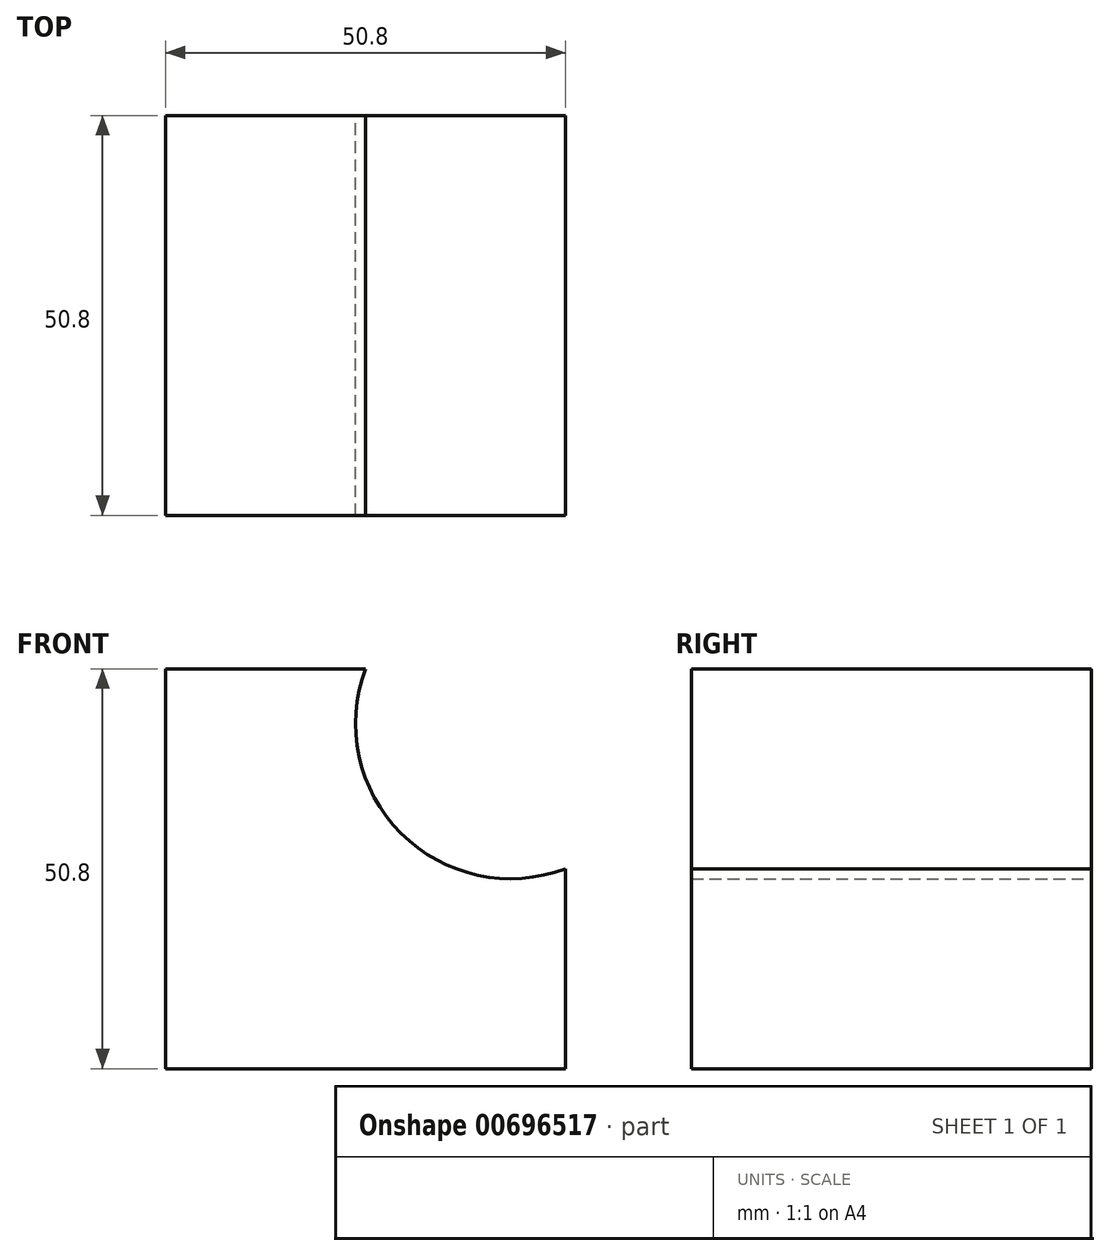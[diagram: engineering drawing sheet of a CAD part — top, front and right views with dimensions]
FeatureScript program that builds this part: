
annotation { "Feature Type Name" : "Feature", "Feature Type Description" : "" }
export const myFeature = defineFeature(function(context is Context, id is Id, definition is map)
    precondition{}
    {
        {
            var Q0;
            Q0=qCreatedBy(makeId("Front.planeOp"),FACE);
            var sketch = newSketch(context, id + "F0", { "sketchPlane" : qUnion([Q0])});
            skLineSegment(sketch, "E0", {"start": v(0, 0) * mm, "end": v(0, -50.8) * mm});
            skLineSegment(sketch, "E1", {"start": v(0, -50.8) * mm, "end": v(50.8, -50.8) * mm});
            skLineSegment(sketch, "E2", {"start": v(50.8, -50.8) * mm, "end": v(50.8, -25.4) * mm});
            skLineSegment(sketch, "E3", {"start": v(0, 0) * mm, "end": v(25.4, 0) * mm});
            skArc(sketch, "E4", {"start": v(25.4, 0) * mm, "mid": v(29.9, -20.9) * mm, "end": v(50.8, -25.4) * mm});
            skSolve(sketch);
        }
        {
            var Q0;
            Q0 = qSketchRegion(id + "F0", true);
            extrude(context, id + "F1", {"entities" : qUnion([Q0]), "depth" : 50.8 * mm, "offsetDistance" : 25.4 * mm});
        }
    });
